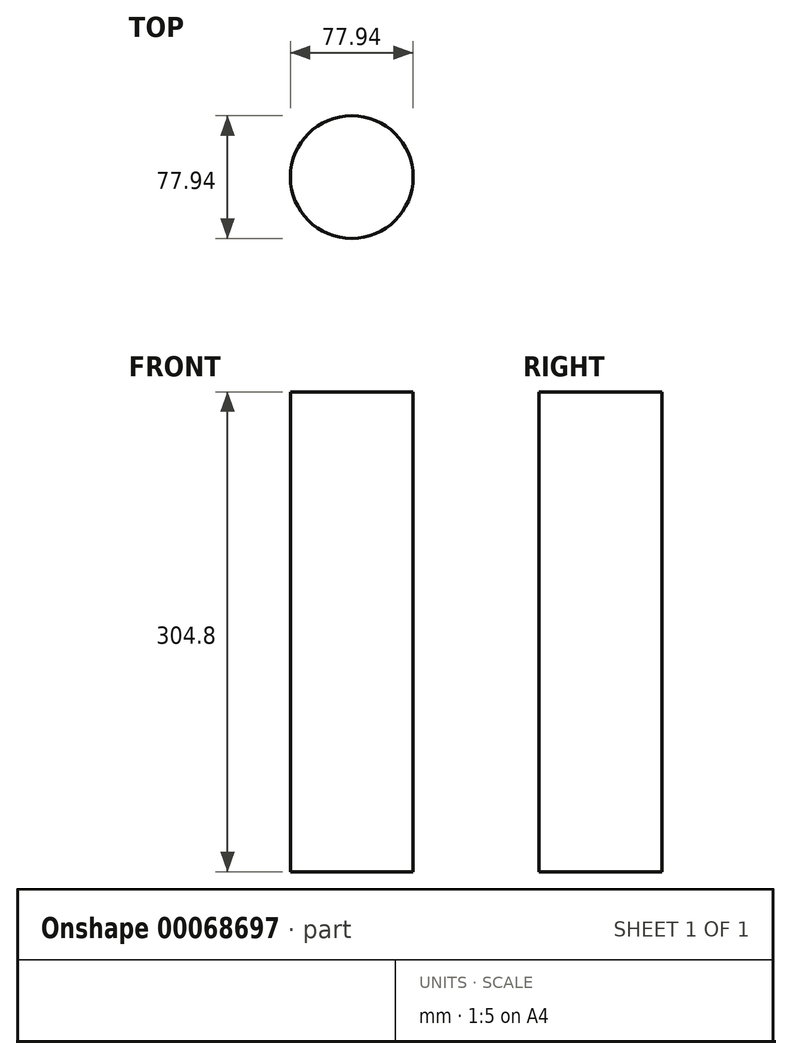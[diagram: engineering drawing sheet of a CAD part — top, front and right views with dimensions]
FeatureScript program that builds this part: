
annotation { "Feature Type Name" : "Feature", "Feature Type Description" : "" }
export const myFeature = defineFeature(function(context is Context, id is Id, definition is map)
    precondition{}
    {
        {
            var Q0;
            Q0=qCreatedBy(makeId("Top.planeOp"),FACE);
            var sketch = newSketch(context, id + "F0", { "sketchPlane" : qUnion([Q0])});
            skCircle(sketch, "E0", {"center": v(0, 0) * mm, "radius": 38.97 * mm});
            skSolve(sketch);
        }
        {
            var Q0;
            Q0 = qSketchRegion(id + "F0", true);
            extrude(context, id + "F1", {"entities" : qUnion([Q0]), "depth" : 304.8 * mm});
        }
    });
